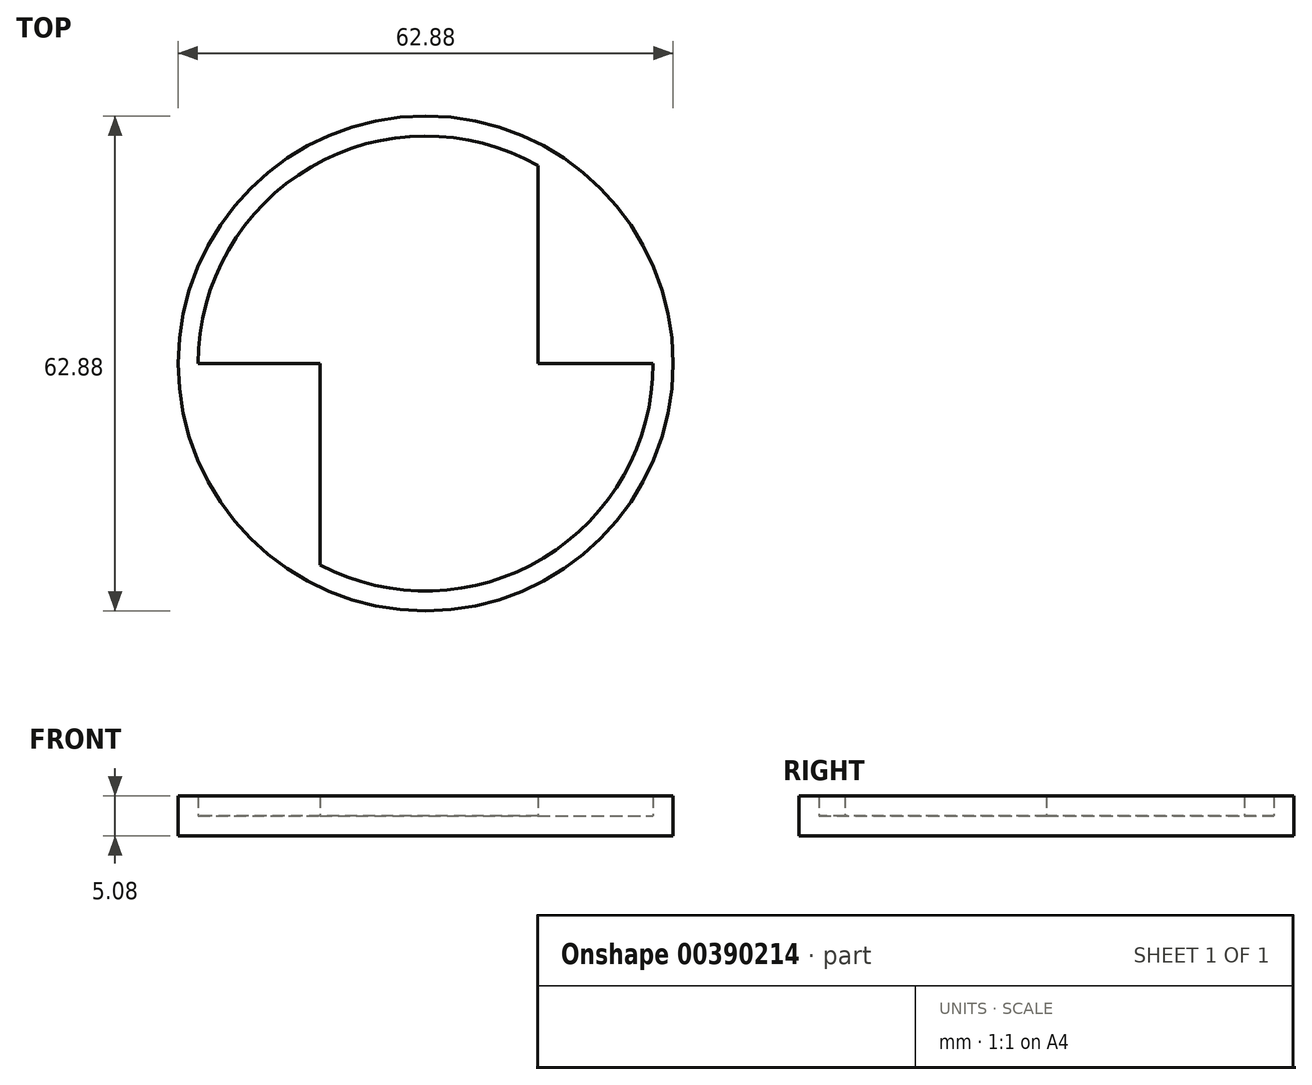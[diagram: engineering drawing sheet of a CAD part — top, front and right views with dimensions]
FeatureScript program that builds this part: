
annotation { "Feature Type Name" : "Feature", "Feature Type Description" : "" }
export const myFeature = defineFeature(function(context is Context, id is Id, definition is map)
    precondition{}
    {
        {
            var Q0;
            Q0=qCreatedBy(makeId("Top.planeOp"),FACE);
            var sketch = newSketch(context, id + "F0", { "sketchPlane" : qUnion([Q0])});
            skCircle(sketch, "E0", {"center": v(0, 0) * mm, "radius": 31.44 * mm});
            skSolve(sketch);
        }
        {
            var Q0;
            Q0=qSketchRegion(id+"F0",true);
            extrude(context, id + "F1", {"entities" : qUnion([Q0]), "depth" : 5.08 * mm});
        }
        {
            var Q0;
            Q0=makeQuery(id+"F1.opExtrude","CAP_FACE",FACE,{"disambiguationData":[OSD([sQuery(id+"F0.wireOp",EDGE,"E0")])],"isStart":false});
            shell(context, id + "F2", {"entities" : qUnion([Q0]), "thickness" : 2.54 * mm});
        }
        {
            var Q0;
            {var subQ0=sQuery(id+"F0.wireOp",EDGE,"E0");Q0=makeQuery(id+"F2.opShell","OFFSET_FACE",FACE,{"disambiguationData":[OSD([subQ0]),TDD([makeQuery(id+"F1.opExtrude","CAP_FACE",FACE,{"disambiguationData":[OSD([subQ0])],"isStart":true})])]});}
            var sketch = newSketch(context, id + "F3", { "sketchPlane" : qUnion([Q0])});
            skLineSegment(sketch, "E1", {"start": v(-28.9, 0) * mm, "end": v(-13.4, 0) * mm});
            skLineSegment(sketch, "E2", {"start": v(-13.4, 0) * mm, "end": v(-13.4, -25.6) * mm});
            skLineSegment(sketch, "E3", {"start": v(14.28, 0) * mm, "end": v(14.28, 25.12) * mm});
            skLineSegment(sketch, "E4", {"start": v(14.28, 0) * mm, "end": v(28.9, 0) * mm});
            skSolve(sketch);
        }
        {
            var Q0;
            Q0=qSketchRegion(id+"F3",true);
            var Q1;
            {var subQ0=sQuery(id+"F3.wireOp",EDGE,"bz3MgF9U-ja5i-29Ou-oI4g-aBsFCOArGGnG");Q1=makeQuery(id+"F3.imprint","IMPRINT",FACE,{"disambiguationData":[TD([[makeQuery(id+"F3.imprint","IMPRINT",EDGE,{"derivedFrom":subQ0}),1.0]])]});}
            var Q2;
            {var subQ0=sQuery(id+"F3.wireOp",EDGE,"E1");Q2=makeQuery(id+"F3.imprint","IMPRINT",FACE,{"disambiguationData":[TD([[makeQuery(id+"F3.imprint","IMPRINT",EDGE,{"derivedFrom":subQ0}),-1.0]])]});}
            var Q3;
            {var subQ0=sQuery(id+"F3.wireOp",EDGE,"E3");Q3=makeQuery(id+"F3.imprint","IMPRINT",FACE,{"disambiguationData":[TD([[makeQuery(id+"F3.imprint","IMPRINT",EDGE,{"derivedFrom":subQ0}),-1.0]])]});}
            extrude(context, id + "F4", {"entities" : qUnion([Q0, Q1, Q2, Q3]), "operationType" : NewBodyOperationType.ADD, "depth" : 2.54 * mm});
        }
    });
